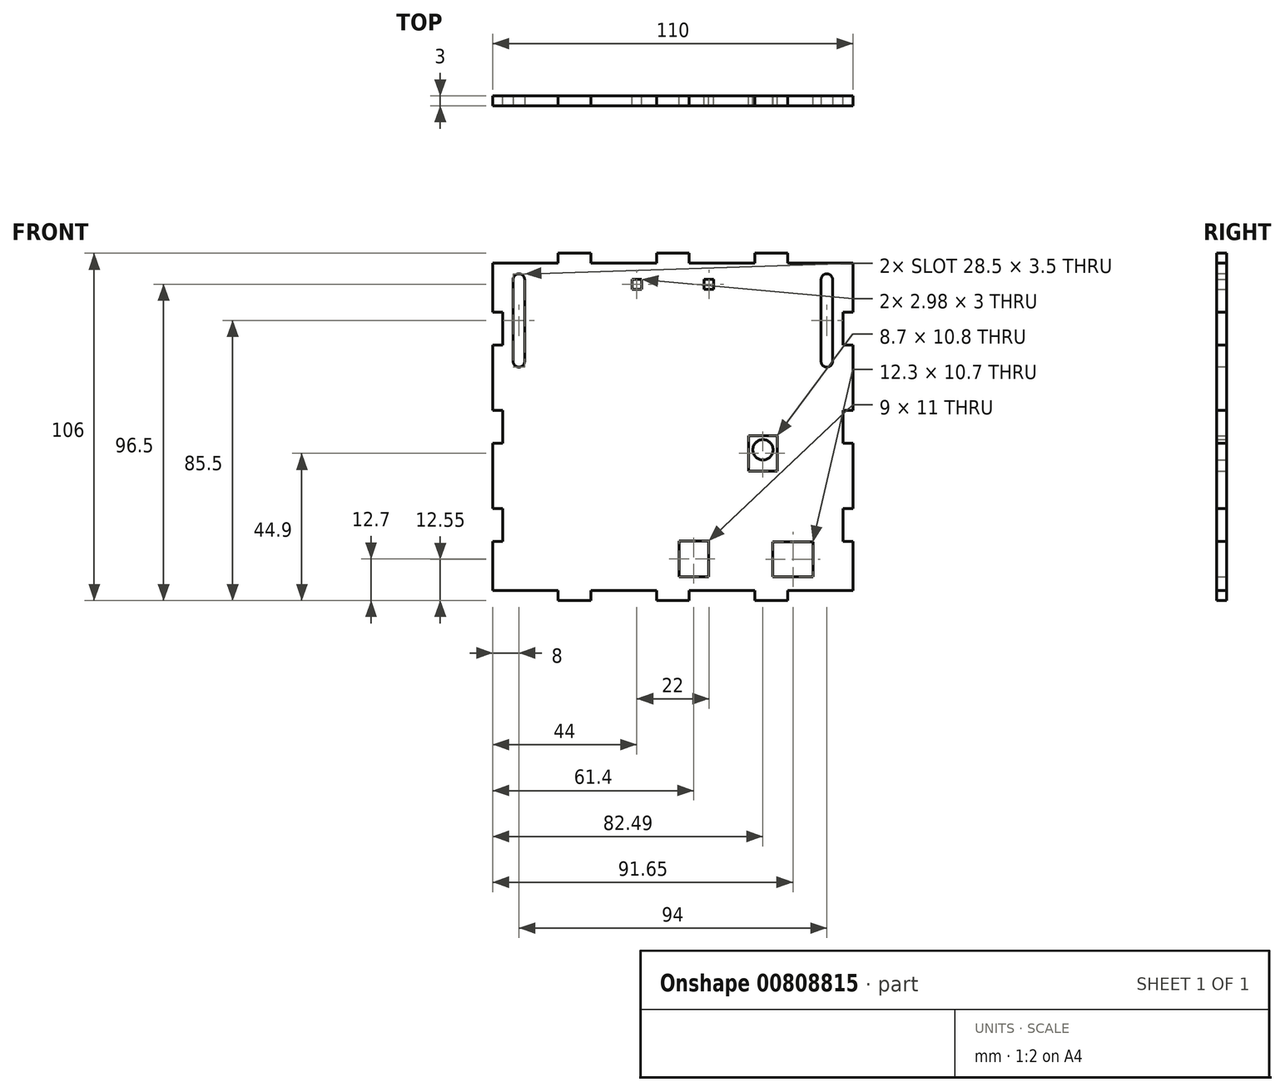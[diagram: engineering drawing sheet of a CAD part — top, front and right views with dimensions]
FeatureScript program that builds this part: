
annotation { "Feature Type Name" : "Feature", "Feature Type Description" : "" }
export const myFeature = defineFeature(function(context is Context, id is Id, definition is map)
    precondition{}
    {
        {
            var Q0;
            Q0=qCreatedBy(makeId("Front.planeOp"),FACE);
            var sketch = newSketch(context, id + "F0", { "sketchPlane" : qUnion([Q0])});
            skLineSegment(sketch, "E0.bottom", {"start": v(55, 50) * mm, "end": v(-55, 50) * mm});
            skLineSegment(sketch, "E0.top", {"start": v(55, -50) * mm, "end": v(-55, -50) * mm});
            skLineSegment(sketch, "E0.left", {"start": v(55, 50) * mm, "end": v(55, -50) * mm});
            skLineSegment(sketch, "E0.right", {"start": v(-55, 50) * mm, "end": v(-55, -50) * mm});
            skPoint(sketch, "E0.middle", {"position": v(0, 0) * mm});
            skLineSegment(sketch, "E1.bottom", {"start": v(-5, 47) * mm, "end": v(5, 47) * mm});
            skLineSegment(sketch, "E1.top", {"start": v(-5, 53) * mm, "end": v(5, 53) * mm});
            skLineSegment(sketch, "E1.left", {"start": v(-5, 47) * mm, "end": v(-5, 53) * mm});
            skLineSegment(sketch, "E1.right", {"start": v(5, 47) * mm, "end": v(5, 53) * mm});
            skPoint(sketch, "E1.middle", {"position": v(0, 50) * mm});
            skLineSegment(sketch, "E2.bottom", {"start": v(25, 47) * mm, "end": v(35, 47) * mm});
            skLineSegment(sketch, "E2.top", {"start": v(25, 53) * mm, "end": v(35, 53) * mm});
            skLineSegment(sketch, "E2.left", {"start": v(25, 47) * mm, "end": v(25, 53) * mm});
            skLineSegment(sketch, "E2.right", {"start": v(35, 47) * mm, "end": v(35, 53) * mm});
            skPoint(sketch, "E2.middle", {"position": v(30, 50) * mm});
            skLineSegment(sketch, "E3.bottom", {"start": v(-35, 47) * mm, "end": v(-25, 47) * mm});
            skLineSegment(sketch, "E3.top", {"start": v(-35, 53) * mm, "end": v(-25, 53) * mm});
            skLineSegment(sketch, "E3.left", {"start": v(-35, 47) * mm, "end": v(-35, 53) * mm});
            skLineSegment(sketch, "E3.right", {"start": v(-25, 47) * mm, "end": v(-25, 53) * mm});
            skPoint(sketch, "E3.middle", {"position": v(-30, 50) * mm});
            skLineSegment(sketch, "E4.1.1", {"start": v(-52, 35) * mm, "end": v(-58, 35) * mm});
            skLineSegment(sketch, "E4.1.2", {"start": v(-58, 25) * mm, "end": v(-58, 35) * mm});
            skLineSegment(sketch, "E4.1.3", {"start": v(-52, -5) * mm, "end": v(-52, 5) * mm});
            skLineSegment(sketch, "E4.1.4", {"start": v(-52, -5) * mm, "end": v(-58, -5) * mm});
            skLineSegment(sketch, "E4.1.5", {"start": v(-58, -5) * mm, "end": v(-58, 5) * mm});
            skLineSegment(sketch, "E4.1.6", {"start": v(-52, 5) * mm, "end": v(-58, 5) * mm});
            skLineSegment(sketch, "E4.1.7", {"start": v(-52, -25) * mm, "end": v(-58, -25) * mm});
            skLineSegment(sketch, "E4.1.8", {"start": v(-58, -35) * mm, "end": v(-58, -25) * mm});
            skLineSegment(sketch, "E4.1.9", {"start": v(-52, -35) * mm, "end": v(-58, -35) * mm});
            skLineSegment(sketch, "E4.1.10", {"start": v(-52, -35) * mm, "end": v(-52, -25) * mm});
            skLineSegment(sketch, "E4.1.11", {"start": v(-52, 25) * mm, "end": v(-58, 25) * mm});
            skLineSegment(sketch, "E4.3.0", {"start": v(52, -25) * mm, "end": v(52, -35) * mm});
            skLineSegment(sketch, "E4.3.1", {"start": v(52, -35) * mm, "end": v(58, -35) * mm});
            skLineSegment(sketch, "E4.3.2", {"start": v(58, -25) * mm, "end": v(58, -35) * mm});
            skLineSegment(sketch, "E4.3.3", {"start": v(52, 5) * mm, "end": v(52, -5) * mm});
            skLineSegment(sketch, "E4.3.4", {"start": v(52, 5) * mm, "end": v(58, 5) * mm});
            skLineSegment(sketch, "E4.3.5", {"start": v(58, 5) * mm, "end": v(58, -5) * mm});
            skLineSegment(sketch, "E4.3.6", {"start": v(52, -5) * mm, "end": v(58, -5) * mm});
            skLineSegment(sketch, "E4.3.7", {"start": v(52, 25) * mm, "end": v(58, 25) * mm});
            skLineSegment(sketch, "E4.3.8", {"start": v(58, 35) * mm, "end": v(58, 25) * mm});
            skLineSegment(sketch, "E4.3.9", {"start": v(52, 35) * mm, "end": v(58, 35) * mm});
            skLineSegment(sketch, "E4.3.10", {"start": v(52, 35) * mm, "end": v(52, 25) * mm});
            skLineSegment(sketch, "E4.3.11", {"start": v(52, -25) * mm, "end": v(58, -25) * mm});
            skPoint(sketch, "E4.center", {"position": v(0, -5) * mm});
            skLineSegment(sketch, "E5", {"start": v(0, 0) * mm, "end": v(11.06, 0) * mm});
            skLineSegment(sketch, "E6.MirrorCS", {"start": v(-35, -47) * mm, "end": v(-25, -47) * mm});
            skLineSegment(sketch, "E7.MirrorCS", {"start": v(-35, -47) * mm, "end": v(-35, -53) * mm});
            skLineSegment(sketch, "E8.MirrorCS", {"start": v(-35, -53) * mm, "end": v(-25, -53) * mm});
            skLineSegment(sketch, "E9.MirrorCS", {"start": v(-25, -47) * mm, "end": v(-25, -53) * mm});
            skLineSegment(sketch, "E10.MirrorCS", {"start": v(-5, -47) * mm, "end": v(-5, -53) * mm});
            skLineSegment(sketch, "E11.MirrorCS", {"start": v(-5, -53) * mm, "end": v(5, -53) * mm});
            skLineSegment(sketch, "E12.MirrorCS", {"start": v(-5, -47) * mm, "end": v(5, -47) * mm});
            skLineSegment(sketch, "E13.MirrorCS", {"start": v(5, -47) * mm, "end": v(5, -53) * mm});
            skLineSegment(sketch, "E14.MirrorCS", {"start": v(35, -47) * mm, "end": v(35, -53) * mm});
            skLineSegment(sketch, "E15.MirrorCS", {"start": v(25, -47) * mm, "end": v(35, -47) * mm});
            skLineSegment(sketch, "E16.MirrorCS", {"start": v(25, -47) * mm, "end": v(25, -53) * mm});
            skLineSegment(sketch, "E17.MirrorCS", {"start": v(25, -53) * mm, "end": v(35, -53) * mm});
            skLineSegment(sketch, "E18", {"start": v(-52, 25) * mm, "end": v(-52, 35) * mm});
            skSolve(sketch);
        }
        {
            var Q0;
            {var subQ5=sQuery(id+"F0.wireOp",EDGE,"E2.top");Q0=makeQuery(id+"F0.imprint","IMPRINT",FACE,{"disambiguationData":[TD([[makeQuery(id+"F0.imprint","IMPRINT",EDGE,{"derivedFrom":subQ5}),-1.0]])]});}
            var Q1;
            {var subQ5=sQuery(id+"F0.wireOp",EDGE,"E1.top");Q1=makeQuery(id+"F0.imprint","IMPRINT",FACE,{"disambiguationData":[TD([[makeQuery(id+"F0.imprint","IMPRINT",EDGE,{"derivedFrom":subQ5}),-1.0]])]});}
            var Q2;
            {var subQ5=sQuery(id+"F0.wireOp",EDGE,"E3.top");Q2=makeQuery(id+"F0.imprint","IMPRINT",FACE,{"disambiguationData":[TD([[makeQuery(id+"F0.imprint","IMPRINT",EDGE,{"derivedFrom":subQ5}),-1.0]])]});}
            var Q3;
            {var subQ5=sQuery(id+"F0.wireOp",EDGE,"E4.2.8");Q3=makeQuery(id+"F0.imprint","IMPRINT",FACE,{"disambiguationData":[TD([[makeQuery(id+"F0.imprint","IMPRINT",EDGE,{"derivedFrom":subQ5}),-1.0]])]});}
            var Q4;
            {var subQ5=sQuery(id+"F0.wireOp",EDGE,"E4.2.5");Q4=makeQuery(id+"F0.imprint","IMPRINT",FACE,{"disambiguationData":[TD([[makeQuery(id+"F0.imprint","IMPRINT",EDGE,{"derivedFrom":subQ5}),-1.0]])]});}
            var Q5;
            {var subQ5=sQuery(id+"F0.wireOp",EDGE,"E4.2.2");Q5=makeQuery(id+"F0.imprint","IMPRINT",FACE,{"disambiguationData":[TD([[makeQuery(id+"F0.imprint","IMPRINT",EDGE,{"derivedFrom":subQ5}),-1.0]])]});}
            var Q6;
            {var subQ5=sQuery(id+"F0.wireOp",EDGE,"E2.bottom");Q6=makeQuery(id+"F0.imprint","IMPRINT",FACE,{"disambiguationData":[TD([[makeQuery(id+"F0.imprint","IMPRINT",EDGE,{"derivedFrom":subQ5}),1.0]])]});}
            var Q7;
            {var subQ5=sQuery(id+"F0.wireOp",EDGE,"E1.bottom");Q7=makeQuery(id+"F0.imprint","IMPRINT",FACE,{"disambiguationData":[TD([[makeQuery(id+"F0.imprint","IMPRINT",EDGE,{"derivedFrom":subQ5}),1.0]])]});}
            var Q8;
            {var subQ5=sQuery(id+"F0.wireOp",EDGE,"E3.bottom");Q8=makeQuery(id+"F0.imprint","IMPRINT",FACE,{"disambiguationData":[TD([[makeQuery(id+"F0.imprint","IMPRINT",EDGE,{"derivedFrom":subQ5}),1.0]])]});}
            var Q9;
            {var subQ5=sQuery(id+"F0.wireOp",EDGE,"E4.2.10");Q9=makeQuery(id+"F0.imprint","IMPRINT",FACE,{"disambiguationData":[TD([[makeQuery(id+"F0.imprint","IMPRINT",EDGE,{"derivedFrom":subQ5}),1.0]])]});}
            var Q10;
            {var subQ5=sQuery(id+"F0.wireOp",EDGE,"E4.2.3");Q10=makeQuery(id+"F0.imprint","IMPRINT",FACE,{"disambiguationData":[TD([[makeQuery(id+"F0.imprint","IMPRINT",EDGE,{"derivedFrom":subQ5}),1.0]])]});}
            var Q11;
            {var subQ5=sQuery(id+"F0.wireOp",EDGE,"E4.2.0");Q11=makeQuery(id+"F0.imprint","IMPRINT",FACE,{"disambiguationData":[TD([[makeQuery(id+"F0.imprint","IMPRINT",EDGE,{"derivedFrom":subQ5}),1.0]])]});}
            var Q12;
            {var subQ37=sQuery(id+"F0.wireOp",EDGE,"E1.bottom");Q12=makeQuery(id+"F0.imprint","IMPRINT",FACE,{"disambiguationData":[TD([[makeQuery(id+"F0.imprint","IMPRINT",EDGE,{"derivedFrom":subQ37}),-1.0]])]});}
            var Q13;
            {var subQ5=sQuery(id+"F0.wireOp",EDGE,"E17.MirrorCS");Q13=makeQuery(id+"F0.imprint","IMPRINT",FACE,{"disambiguationData":[TD([[makeQuery(id+"F0.imprint","IMPRINT",EDGE,{"derivedFrom":subQ5}),1.0]])]});}
            var Q14;
            {var subQ5=sQuery(id+"F0.wireOp",EDGE,"E15.MirrorCS");Q14=makeQuery(id+"F0.imprint","IMPRINT",FACE,{"disambiguationData":[TD([[makeQuery(id+"F0.imprint","IMPRINT",EDGE,{"derivedFrom":subQ5}),-1.0]])]});}
            var Q15;
            {var subQ5=sQuery(id+"F0.wireOp",EDGE,"E12.MirrorCS");Q15=makeQuery(id+"F0.imprint","IMPRINT",FACE,{"disambiguationData":[TD([[makeQuery(id+"F0.imprint","IMPRINT",EDGE,{"derivedFrom":subQ5}),-1.0]])]});}
            var Q16;
            {var subQ5=sQuery(id+"F0.wireOp",EDGE,"E11.MirrorCS");Q16=makeQuery(id+"F0.imprint","IMPRINT",FACE,{"disambiguationData":[TD([[makeQuery(id+"F0.imprint","IMPRINT",EDGE,{"derivedFrom":subQ5}),1.0]])]});}
            var Q17;
            {var subQ5=sQuery(id+"F0.wireOp",EDGE,"E6.MirrorCS");Q17=makeQuery(id+"F0.imprint","IMPRINT",FACE,{"disambiguationData":[TD([[makeQuery(id+"F0.imprint","IMPRINT",EDGE,{"derivedFrom":subQ5}),-1.0]])]});}
            var Q18;
            {var subQ5=sQuery(id+"F0.wireOp",EDGE,"E8.MirrorCS");Q18=makeQuery(id+"F0.imprint","IMPRINT",FACE,{"disambiguationData":[TD([[makeQuery(id+"F0.imprint","IMPRINT",EDGE,{"derivedFrom":subQ5}),1.0]])]});}
            extrude(context, id + "F1", {"entities" : qUnion([Q0, Q1, Q2, Q3, Q4, Q5, Q6, Q7, Q8, Q9, Q10, Q11, Q12, Q13, Q14, Q15, Q16, Q17, Q18]), "depth" : 3 * mm, "offsetDistance" : 25 * mm});
        }
        {
            var Q0;
            Q0=makeQuery(id+"F1.opExtrude","CAP_FACE",FACE,{"disambiguationData":[OSD([sQuery(id+"F0.wireOp",EDGE,"E0.bottom"),sQuery(id+"F0.wireOp",EDGE,"E0.top"),sQuery(id+"F0.wireOp",EDGE,"E0.left"),sQuery(id+"F0.wireOp",EDGE,"E0.right"),sQuery(id+"F0.wireOp",EDGE,"E1.top"),sQuery(id+"F0.wireOp",EDGE,"E1.left"),sQuery(id+"F0.wireOp",EDGE,"E1.right"),sQuery(id+"F0.wireOp",EDGE,"E2.top"),sQuery(id+"F0.wireOp",EDGE,"E2.left"),sQuery(id+"F0.wireOp",EDGE,"E2.right"),sQuery(id+"F0.wireOp",EDGE,"E3.top"),sQuery(id+"F0.wireOp",EDGE,"E3.left"),sQuery(id+"F0.wireOp",EDGE,"E3.right"),sQuery(id+"F0.wireOp",EDGE,"E4.1.0"),sQuery(id+"F0.wireOp",EDGE,"E4.1.1"),sQuery(id+"F0.wireOp",EDGE,"E4.1.3"),sQuery(id+"F0.wireOp",EDGE,"E4.1.4"),sQuery(id+"F0.wireOp",EDGE,"E4.1.6"),sQuery(id+"F0.wireOp",EDGE,"E4.1.7"),sQuery(id+"F0.wireOp",EDGE,"E4.1.9"),sQuery(id+"F0.wireOp",EDGE,"E4.1.10"),sQuery(id+"F0.wireOp",EDGE,"E4.1.11"),sQuery(id+"F0.wireOp",EDGE,"E4.2.1"),sQuery(id+"F0.wireOp",EDGE,"E4.2.2"),sQuery(id+"F0.wireOp",EDGE,"E4.2.4"),sQuery(id+"F0.wireOp",EDGE,"E4.2.5"),sQuery(id+"F0.wireOp",EDGE,"E4.2.6"),sQuery(id+"F0.wireOp",EDGE,"E4.2.7"),sQuery(id+"F0.wireOp",EDGE,"E4.2.8"),sQuery(id+"F0.wireOp",EDGE,"E4.2.9"),sQuery(id+"F0.wireOp",EDGE,"E4.2.11"),sQuery(id+"F0.wireOp",EDGE,"E4.3.0"),sQuery(id+"F0.wireOp",EDGE,"E4.3.1"),sQuery(id+"F0.wireOp",EDGE,"E4.3.3"),sQuery(id+"F0.wireOp",EDGE,"E4.3.4"),sQuery(id+"F0.wireOp",EDGE,"E4.3.6"),sQuery(id+"F0.wireOp",EDGE,"E4.3.7"),sQuery(id+"F0.wireOp",EDGE,"E4.3.9"),sQuery(id+"F0.wireOp",EDGE,"E4.3.10"),sQuery(id+"F0.wireOp",EDGE,"E4.3.11")])],"isStart":true});
            var sketch = newSketch(context, id + "F2", { "sketchPlane" : qUnion([Q0])});
            skLineSegment(sketch, "E19.bottom", {"start": v(-9.5, 42) * mm, "end": v(-12.49, 42) * mm});
            skLineSegment(sketch, "E19.top", {"start": v(-9.5, 45) * mm, "end": v(-12.49, 45) * mm});
            skLineSegment(sketch, "E19.left", {"start": v(-9.5, 42) * mm, "end": v(-9.5, 45) * mm});
            skLineSegment(sketch, "E19.right", {"start": v(-12.49, 42) * mm, "end": v(-12.49, 45) * mm});
            skPoint(sketch, "E19.middle", {"position": v(-11, 43.5) * mm});
            skLineSegment(sketch, "E20.bottom", {"start": v(-42.8, -45.8) * mm, "end": v(-30.5, -45.8) * mm});
            skLineSegment(sketch, "E20.top", {"start": v(-42.8, -35.1) * mm, "end": v(-30.5, -35.1) * mm});
            skLineSegment(sketch, "E20.left", {"start": v(-42.8, -45.8) * mm, "end": v(-42.8, -35.1) * mm});
            skLineSegment(sketch, "E20.right", {"start": v(-30.5, -45.8) * mm, "end": v(-30.5, -35.1) * mm});
            skPoint(sketch, "E20.middle", {"position": v(-36.65, -40.45) * mm});
            skLineSegment(sketch, "E21.bottom", {"start": v(-10.9, -34.8) * mm, "end": v(-1.9, -34.8) * mm});
            skLineSegment(sketch, "E21.top", {"start": v(-10.9, -45.8) * mm, "end": v(-1.9, -45.8) * mm});
            skLineSegment(sketch, "E21.left", {"start": v(-10.9, -34.8) * mm, "end": v(-10.9, -45.8) * mm});
            skLineSegment(sketch, "E21.right", {"start": v(-1.9, -34.8) * mm, "end": v(-1.9, -45.8) * mm});
            skPoint(sketch, "E21.middle", {"position": v(-6.4, -40.3) * mm});
            skLineSegment(sketch, "E22", {"start": v(0, 53) * mm, "end": v(0, 42.79) * mm});
            skLineSegment(sketch, "E23.MirrorCS", {"start": v(12.5, 42) * mm, "end": v(12.5, 45) * mm});
            skLineSegment(sketch, "E24.MirrorCS", {"start": v(9.51, 42) * mm, "end": v(9.51, 45) * mm});
            skLineSegment(sketch, "E25.MirrorCS", {"start": v(9.5, 42) * mm, "end": v(12.49, 42) * mm});
            skLineSegment(sketch, "E26.MirrorCS", {"start": v(9.51, 45) * mm, "end": v(12.5, 45) * mm});
            skPoint(sketch, "E27.MirrorP", {"position": v(11, 43.5) * mm});
            skLineSegment(sketch, "E28", {"start": v(0, 0) * mm, "end": v(0, 5.7) * mm});
            skCircle(sketch, "E29", {"center": v(-27.49, -7) * mm, "radius": 3.1 * mm});
            skLineSegment(sketch, "E30.bottom", {"start": v(-31.84, -2.7) * mm, "end": v(-23.14, -2.7) * mm});
            skLineSegment(sketch, "E30.top", {"start": v(-31.84, -11.3) * mm, "end": v(-23.14, -11.3) * mm});
            skLineSegment(sketch, "E30.left", {"start": v(-31.84, -2.7) * mm, "end": v(-31.84, -11.3) * mm});
            skLineSegment(sketch, "E30.right", {"start": v(-23.14, -2.7) * mm, "end": v(-23.14, -11.3) * mm});
            skLineSegment(sketch, "E31.bottom", {"start": v(-31.84, -6.95) * mm, "end": v(-23.14, -6.95) * mm});
            skLineSegment(sketch, "E31.top", {"start": v(-31.84, -13.5) * mm, "end": v(-23.14, -13.5) * mm});
            skLineSegment(sketch, "E31.left", {"start": v(-31.84, -6.95) * mm, "end": v(-31.84, -13.5) * mm});
            skLineSegment(sketch, "E31.right", {"start": v(-23.14, -6.95) * mm, "end": v(-23.14, -13.5) * mm});
            skPoint(sketch, "E31.middle", {"position": v(-27.49, -10.23) * mm});
            skPoint(sketch, "E31.middle.positionSnap0", {"position": v(-27.49, -11.3) * mm});
            skPoint(sketch, "E31.centerSnap0", {"position": v(-27.49, -11.3) * mm});
            skSolve(sketch);
        }
        {
            var Q0;
            Q0=qSketchRegion(id+"F2",true);
            var Q1;
            Q1=makeQuery(id+"F1.opExtrude","CAP_FACE",FACE,{"disambiguationData":[OSD([sQuery(id+"F0.wireOp",EDGE,"E0.bottom"),sQuery(id+"F0.wireOp",EDGE,"E0.top"),sQuery(id+"F0.wireOp",EDGE,"E0.left"),sQuery(id+"F0.wireOp",EDGE,"E0.right"),sQuery(id+"F0.wireOp",EDGE,"E1.top"),sQuery(id+"F0.wireOp",EDGE,"E1.left"),sQuery(id+"F0.wireOp",EDGE,"E1.right"),sQuery(id+"F0.wireOp",EDGE,"E2.top"),sQuery(id+"F0.wireOp",EDGE,"E2.left"),sQuery(id+"F0.wireOp",EDGE,"E2.right"),sQuery(id+"F0.wireOp",EDGE,"E3.top"),sQuery(id+"F0.wireOp",EDGE,"E3.left"),sQuery(id+"F0.wireOp",EDGE,"E3.right"),sQuery(id+"F0.wireOp",EDGE,"E4.1.0"),sQuery(id+"F0.wireOp",EDGE,"E4.1.1"),sQuery(id+"F0.wireOp",EDGE,"E4.1.3"),sQuery(id+"F0.wireOp",EDGE,"E4.1.4"),sQuery(id+"F0.wireOp",EDGE,"E4.1.6"),sQuery(id+"F0.wireOp",EDGE,"E4.1.7"),sQuery(id+"F0.wireOp",EDGE,"E4.1.9"),sQuery(id+"F0.wireOp",EDGE,"E4.1.10"),sQuery(id+"F0.wireOp",EDGE,"E4.1.11"),sQuery(id+"F0.wireOp",EDGE,"E4.3.0"),sQuery(id+"F0.wireOp",EDGE,"E4.3.1"),sQuery(id+"F0.wireOp",EDGE,"E4.3.3"),sQuery(id+"F0.wireOp",EDGE,"E4.3.4"),sQuery(id+"F0.wireOp",EDGE,"E4.3.6"),sQuery(id+"F0.wireOp",EDGE,"E4.3.7"),sQuery(id+"F0.wireOp",EDGE,"E4.3.9"),sQuery(id+"F0.wireOp",EDGE,"E4.3.10"),sQuery(id+"F0.wireOp",EDGE,"E4.3.11"),sQuery(id+"F0.wireOp",EDGE,"E6.MirrorCS"),sQuery(id+"F0.wireOp",EDGE,"E7.MirrorCS"),sQuery(id+"F0.wireOp",EDGE,"E9.MirrorCS"),sQuery(id+"F0.wireOp",EDGE,"E10.MirrorCS"),sQuery(id+"F0.wireOp",EDGE,"E12.MirrorCS"),sQuery(id+"F0.wireOp",EDGE,"E13.MirrorCS"),sQuery(id+"F0.wireOp",EDGE,"E14.MirrorCS"),sQuery(id+"F0.wireOp",EDGE,"E15.MirrorCS"),sQuery(id+"F0.wireOp",EDGE,"E16.MirrorCS")])],"isStart":false});
            extrude(context, id + "F3", {"entities" : qUnion([Q0, Q1]), "operationType" : NewBodyOperationType.REMOVE, "oppositeDirection" : true, "depth" : 25 * mm, "offsetDistance" : 25 * mm});
        }
        {
            var Q0;
            Q0=makeQuery(id+"F1.opExtrude","CAP_FACE",FACE,{"disambiguationData":[OSD([sQuery(id+"F0.wireOp",EDGE,"E0.bottom"),sQuery(id+"F0.wireOp",EDGE,"E0.top"),sQuery(id+"F0.wireOp",EDGE,"E0.left"),sQuery(id+"F0.wireOp",EDGE,"E0.right"),sQuery(id+"F0.wireOp",EDGE,"E1.top"),sQuery(id+"F0.wireOp",EDGE,"E1.left"),sQuery(id+"F0.wireOp",EDGE,"E1.right"),sQuery(id+"F0.wireOp",EDGE,"E2.top"),sQuery(id+"F0.wireOp",EDGE,"E2.left"),sQuery(id+"F0.wireOp",EDGE,"E2.right"),sQuery(id+"F0.wireOp",EDGE,"E3.top"),sQuery(id+"F0.wireOp",EDGE,"E3.left"),sQuery(id+"F0.wireOp",EDGE,"E3.right"),sQuery(id+"F0.wireOp",EDGE,"E4.1.0"),sQuery(id+"F0.wireOp",EDGE,"E4.1.1"),sQuery(id+"F0.wireOp",EDGE,"E4.1.3"),sQuery(id+"F0.wireOp",EDGE,"E4.1.4"),sQuery(id+"F0.wireOp",EDGE,"E4.1.6"),sQuery(id+"F0.wireOp",EDGE,"E4.1.7"),sQuery(id+"F0.wireOp",EDGE,"E4.1.9"),sQuery(id+"F0.wireOp",EDGE,"E4.1.10"),sQuery(id+"F0.wireOp",EDGE,"E4.1.11"),sQuery(id+"F0.wireOp",EDGE,"E4.2.1"),sQuery(id+"F0.wireOp",EDGE,"E4.2.2"),sQuery(id+"F0.wireOp",EDGE,"E4.2.4"),sQuery(id+"F0.wireOp",EDGE,"E4.2.5"),sQuery(id+"F0.wireOp",EDGE,"E4.2.6"),sQuery(id+"F0.wireOp",EDGE,"E4.2.7"),sQuery(id+"F0.wireOp",EDGE,"E4.2.8"),sQuery(id+"F0.wireOp",EDGE,"E4.2.9"),sQuery(id+"F0.wireOp",EDGE,"E4.2.11"),sQuery(id+"F0.wireOp",EDGE,"E4.3.0"),sQuery(id+"F0.wireOp",EDGE,"E4.3.1"),sQuery(id+"F0.wireOp",EDGE,"E4.3.3"),sQuery(id+"F0.wireOp",EDGE,"E4.3.4"),sQuery(id+"F0.wireOp",EDGE,"E4.3.6"),sQuery(id+"F0.wireOp",EDGE,"E4.3.7"),sQuery(id+"F0.wireOp",EDGE,"E4.3.9"),sQuery(id+"F0.wireOp",EDGE,"E4.3.10"),sQuery(id+"F0.wireOp",EDGE,"E4.3.11")])],"isStart":false});
            var sketch = newSketch(context, id + "F4", { "sketchPlane" : qUnion([Q0])});
            skLineSegment(sketch, "E32", {"start": v(-47, 45) * mm, "end": v(-47, 20) * mm});
            skLineSegment(sketch, "E33", {"start": v(0, 53) * mm, "end": v(0, 46.35) * mm});
            skArc(sketch, "E34.0.startCap", {"start": v(-48.75, 45) * mm, "mid": v(-47, 46.75) * mm, "end": v(-45.25, 45) * mm});
            skArc(sketch, "E34.0.endCap", {"start": v(-45.25, 20) * mm, "mid": v(-47, 18.25) * mm, "end": v(-48.75, 20) * mm});
            skLineSegment(sketch, "E34.0.left", {"start": v(-45.25, 45) * mm, "end": v(-45.25, 20) * mm});
            skLineSegment(sketch, "E34.0.right", {"start": v(-48.75, 45) * mm, "end": v(-48.75, 20) * mm});
            skLineSegment(sketch, "E35.MirrorCS", {"start": v(45.25, 45) * mm, "end": v(45.25, 20) * mm});
            skArc(sketch, "E36.MirrorCS", {"start": v(48.75, 45) * mm, "mid": v(47, 46.75) * mm, "end": v(45.25, 45) * mm});
            skLineSegment(sketch, "E37.MirrorCS", {"start": v(48.75, 45) * mm, "end": v(48.75, 20) * mm});
            skArc(sketch, "E38.MirrorCS", {"start": v(45.25, 20) * mm, "mid": v(47, 18.25) * mm, "end": v(48.75, 20) * mm});
            skSolve(sketch);
        }
        {
            var Q0;
            Q0=qSketchRegion(id+"F4",true);
            extrude(context, id + "F5", {"entities" : qUnion([Q0]), "operationType" : NewBodyOperationType.REMOVE, "oppositeDirection" : true, "depth" : 25 * mm, "offsetDistance" : 25 * mm});
        }
    });
